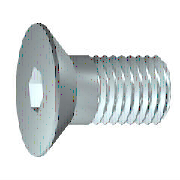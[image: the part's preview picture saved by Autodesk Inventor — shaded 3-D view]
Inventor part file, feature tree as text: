
AUTODESK INVENTOR PART (.ipt)
format: ipt  version: 2022 (Build 260153000, 153)  size: 199,168 bytes
history: native  units: mm (DEFAULTED — no unit token found)
features: other x4, sketch x3, fillet x1, chamfer x1
ambient origin geometry x8: Origin, YZ Plane, XZ Plane, XY Plane, X Axis, Y Axis, Z Axis, Center Point
bodies: Solid1 (feature_tree)
feature tree (9):
  sketch  "Sketch1"  dims[d2=3.0mm]
  other  "WorkPoint1"
  sketch  "Sketch2"  dims[d4=1.5mm]
  fillet  "Fillet1"  [1 undecoded]
  chamfer  "Chamfer1"  Angle=360.0deg  [1 undecoded]
  other  "MSC_A1"
  other  "MSC_PF1"
  other  "MSC_PT1"
  sketch  "Sketch3"  dims[d6=8.0mm d8=360.0deg d9=0.0mm d10=2.0mm d11=4.0mm d12=120.0deg d13=120.0deg d14=120.0deg d15=120.0deg d16=2.5mm d17=0.0mm d18=0.3mm d19=0.5mm d20=45.0deg d35=0.0mm d37=0.0mm d38=0.0mm d39=0.5mm d40=0.0mm d41=0.0mm d42=0.0mm d43=45.0deg d44=6.0mm d45=3.0mm d46=8.0mm d47=0.0mm d48=0.0mm]
note: 2 required parameter values undecoded (feature->parameter linkage not recoverable at this tier; creation-order binding heuristic only, values carry confidence <= 0.55)
